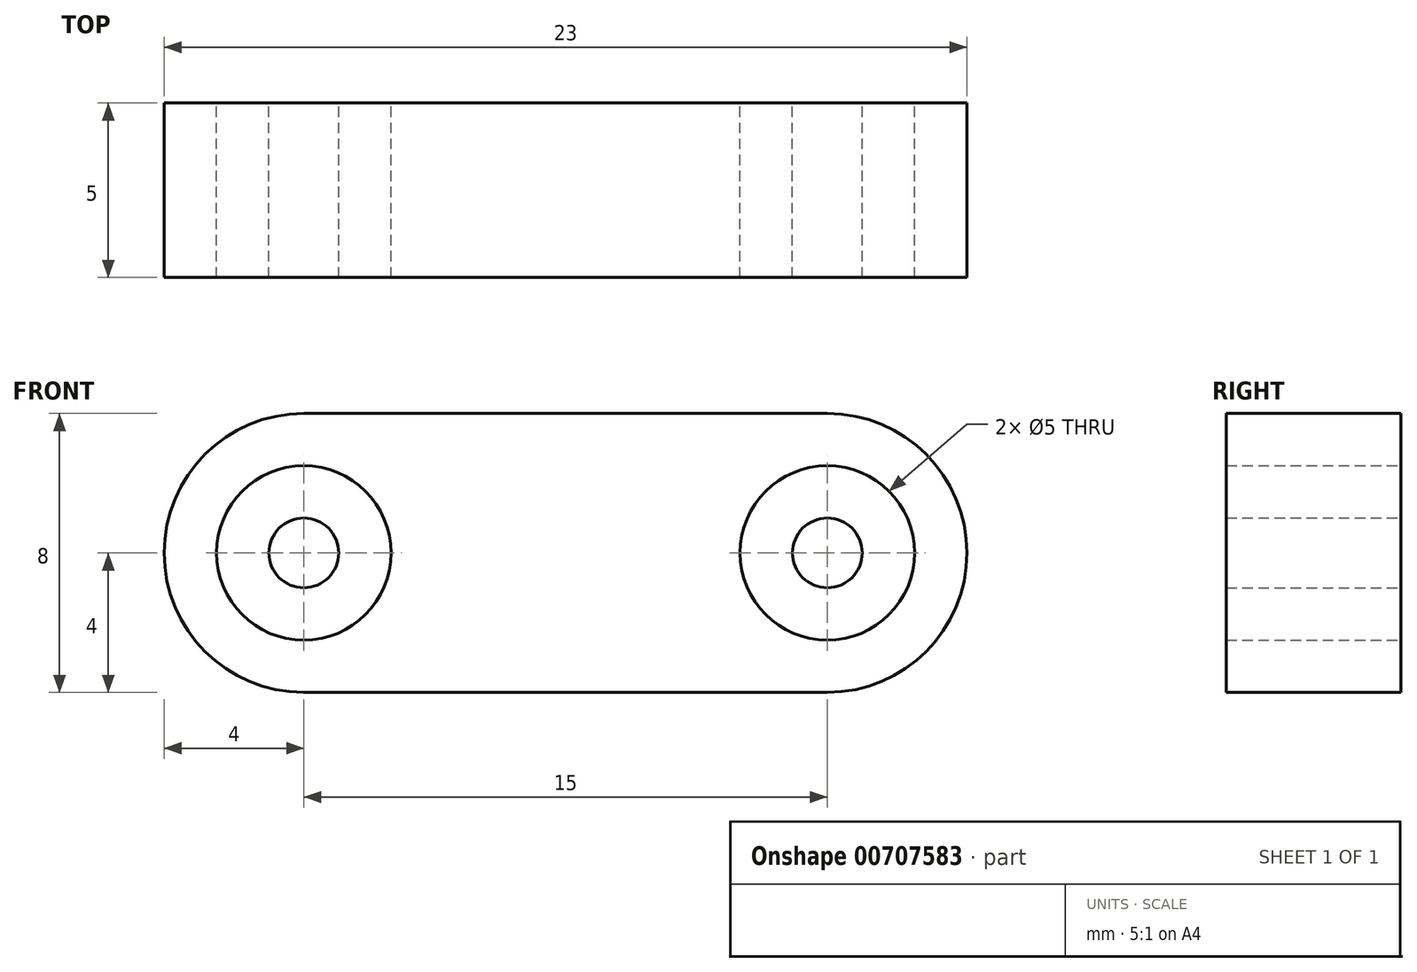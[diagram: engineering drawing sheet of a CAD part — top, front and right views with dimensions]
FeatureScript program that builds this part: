
annotation { "Feature Type Name" : "Feature", "Feature Type Description" : "" }
export const myFeature = defineFeature(function(context is Context, id is Id, definition is map)
    precondition{}
    {
        {
            var Q0;
            Q0=qCreatedBy(makeId("Front.planeOp"),FACE);
            var sketch = newSketch(context, id + "F0", { "sketchPlane" : qUnion([Q0])});
            skArc(sketch, "E0", {"start": v(0, 4) * mm, "mid": v(-4, 0) * mm, "end": v(0, -4) * mm});
            skCircle(sketch, "E1", {"center": v(0, 0) * mm, "radius": 2.5 * mm});
            skCircle(sketch, "E2", {"center": v(0, 0) * mm, "radius": 1 * mm});
            skLineSegment(sketch, "E3", {"start": v(0, 0) * mm, "end": v(15, 0) * mm});
            skArc(sketch, "E4", {"start": v(15, -4) * mm, "mid": v(19, 0) * mm, "end": v(15, 4) * mm});
            skCircle(sketch, "E5", {"center": v(15, 0) * mm, "radius": 2.5 * mm});
            skCircle(sketch, "E6", {"center": v(15, 0) * mm, "radius": 1 * mm});
            skLineSegment(sketch, "E7", {"start": v(0, 4) * mm, "end": v(15, 4) * mm});
            skLineSegment(sketch, "E8", {"start": v(0, -4) * mm, "end": v(15, -4) * mm});
            skSolve(sketch);
        }
        {
            var Q0;
            Q0=makeQuery(id+"F0.imprint","IMPRINT",FACE,{"disambiguationData":[TD([[makeQuery(id+"F0.imprint","IMPRINT",EDGE,{"derivedFrom":sQuery(id+"F0.wireOp",EDGE,"E0")}),1.0]])]});
            var Q1;
            Q1=makeQuery(id+"F0.imprint","IMPRINT",FACE,{"disambiguationData":[TD([[makeQuery(id+"F0.imprint","IMPRINT",EDGE,{"derivedFrom":sQuery(id+"F0.wireOp",EDGE,"E2")}),1.0]])]});
            var Q2;
            Q2=makeQuery(id+"F0.imprint","IMPRINT",FACE,{"disambiguationData":[TD([[makeQuery(id+"F0.imprint","IMPRINT",EDGE,{"derivedFrom":sQuery(id+"F0.wireOp",EDGE,"E6")}),1.0]])]});
            extrude(context, id + "F1", {"entities" : qUnion([Q0, Q1, Q2]), "depth" : 5 * mm, "offsetDistance" : 25.4 * mm});
        }
    });
